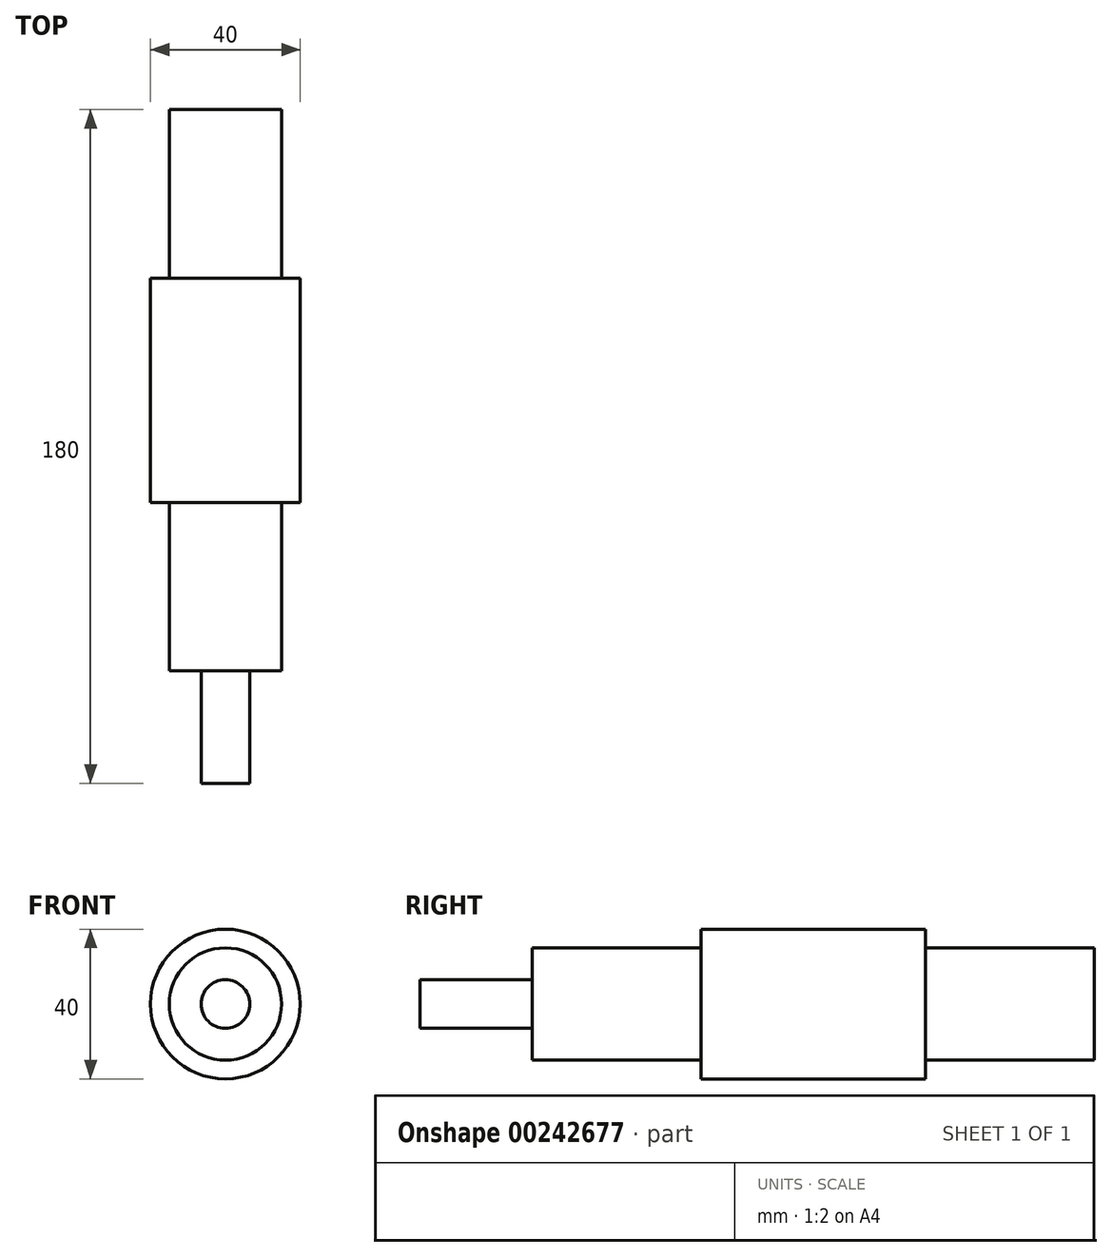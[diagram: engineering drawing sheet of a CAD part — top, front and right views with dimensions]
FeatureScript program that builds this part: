
annotation { "Feature Type Name" : "Feature", "Feature Type Description" : "" }
export const myFeature = defineFeature(function(context is Context, id is Id, definition is map)
    precondition{}
    {
        {
            var Q0;
            Q0=qCreatedBy(makeId("Front.planeOp"),FACE);
            var sketch = newSketch(context, id + "F0", { "sketchPlane" : qUnion([Q0])});
            skCircle(sketch, "E0", {"center": v(0, 0) * mm, "radius": 20 * mm});
            skSolve(sketch);
        }
        {
            var Q0;
            Q0 = qSketchRegion(id + "F0", true);
            extrude(context, id + "F1", {"entities" : qUnion([Q0]), "depth" : 60 * mm});
        }
        {
            var Q0;
            Q0=makeQuery(id+"F1.opExtrude","CAP_FACE",FACE,{"disambiguationData":[OSD([sQuery(id+"F0.wireOp",EDGE,"E0")])],"isStart":false});
            var sketch = newSketch(context, id + "F2", { "sketchPlane" : qUnion([Q0])});
            skCircle(sketch, "E1", {"center": v(0, 0) * mm, "radius": 15 * mm});
            skSolve(sketch);
        }
        {
            var Q0;
            Q0=makeQuery(id+"F1.opExtrude","CAP_FACE",FACE,{"disambiguationData":[OSD([sQuery(id+"F0.wireOp",EDGE,"E0")])],"isStart":true});
            var sketch = newSketch(context, id + "F3", { "sketchPlane" : qUnion([Q0])});
            skCircle(sketch, "E2", {"center": v(0, 0) * mm, "radius": 15 * mm});
            skSolve(sketch);
        }
        {
            var Q0;
            Q0 = qSketchRegion(id + "F3", true);
            extrude(context, id + "F4", {"entities" : qUnion([Q0]), "operationType" : NewBodyOperationType.ADD, "depth" : 45 * mm});
        }
        {
            var Q0;
            Q0=makeQuery(id+"F2.imprint","IMPRINT",FACE,{"disambiguationData":[TD([[makeQuery(id+"F2.imprint","IMPRINT",EDGE,{"derivedFrom":sQuery(id+"F2.wireOp",EDGE,"E1")}),1.0]])]});
            extrude(context, id + "F5", {"entities" : qUnion([Q0]), "operationType" : NewBodyOperationType.ADD, "depth" : 45 * mm});
        }
        {
            var Q0;
            Q0=makeQuery(id+"F5.opExtrude","CAP_FACE",FACE,{"disambiguationData":[OSD([sQuery(id+"F2.wireOp",EDGE,"E1")])],"isStart":false});
            var sketch = newSketch(context, id + "F6", { "sketchPlane" : qUnion([Q0])});
            skCircle(sketch, "E3", {"center": v(0, 0) * mm, "radius": 6.5 * mm});
            skSolve(sketch);
        }
        {
            var Q0;
            Q0=makeQuery(id+"F6.imprint","IMPRINT",FACE,{"disambiguationData":[TD([[makeQuery(id+"F6.imprint","IMPRINT",EDGE,{"derivedFrom":sQuery(id+"F6.wireOp",EDGE,"E3")}),1.0]])]});
            extrude(context, id + "F7", {"entities" : qUnion([Q0]), "operationType" : NewBodyOperationType.ADD, "depth" : 30 * mm});
        }
    });
